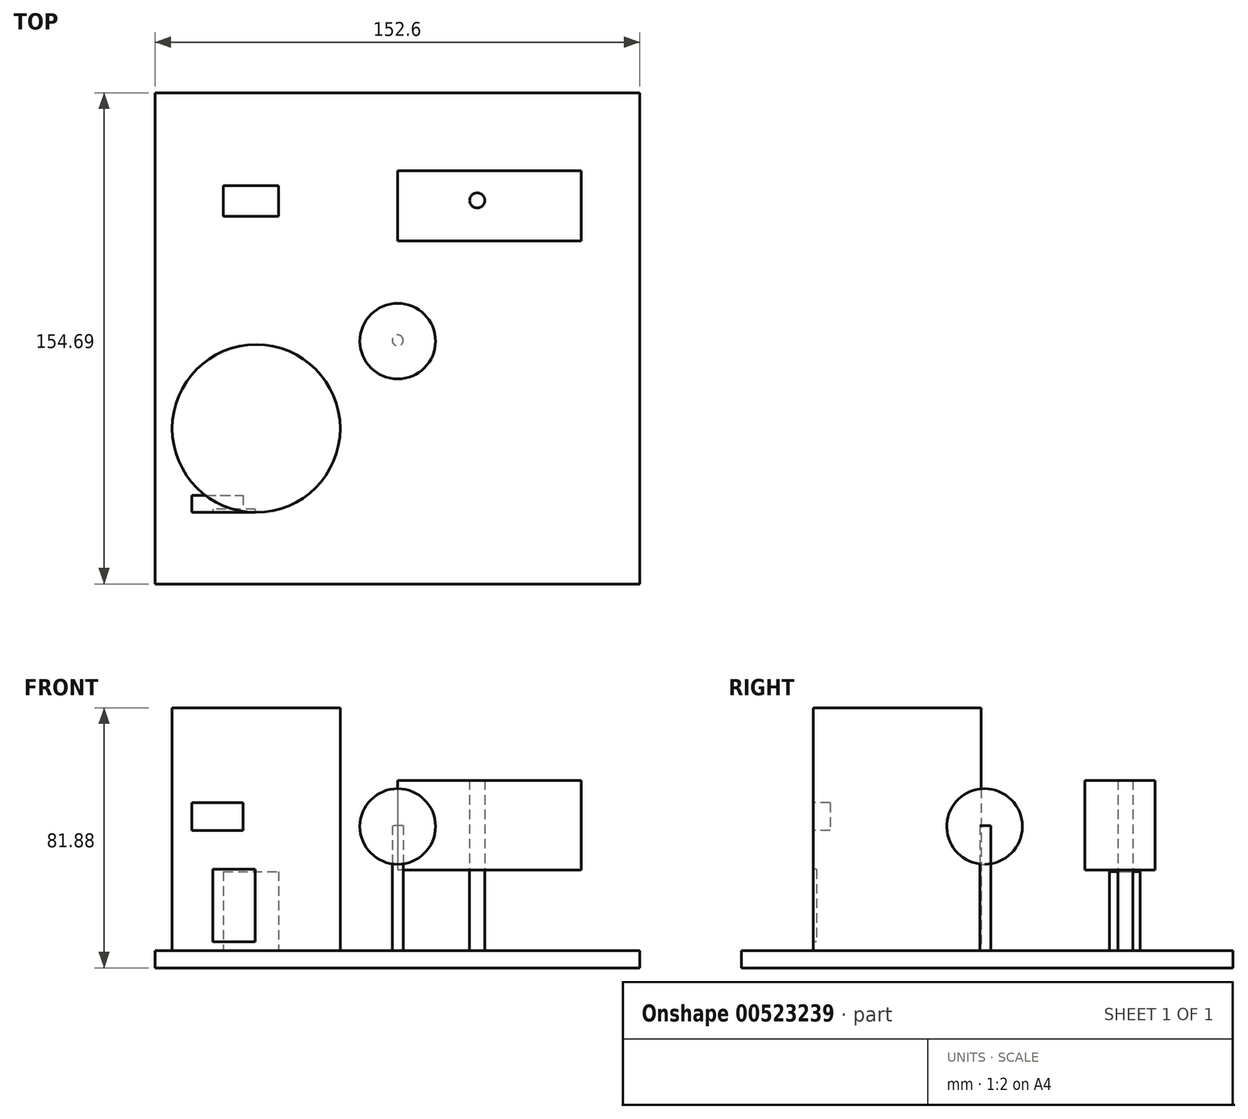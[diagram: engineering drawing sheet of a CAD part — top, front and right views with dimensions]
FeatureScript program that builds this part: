
annotation { "Feature Type Name" : "Feature", "Feature Type Description" : "" }
export const myFeature = defineFeature(function(context is Context, id is Id, definition is map)
    precondition{}
    {
        {
            var Q0;
            Q0=qCreatedBy(makeId("Front.planeOp"),FACE);
            var sketch = newSketch(context, id + "F0", { "sketchPlane" : qUnion([Q0])});
            skLineSegment(sketch, "E0.bottom", {"start": v(76.2, 0) * mm, "end": v(-76.39, 0) * mm});
            skLineSegment(sketch, "E0.top", {"start": v(76.2, -5.43) * mm, "end": v(-76.39, -5.43) * mm});
            skLineSegment(sketch, "E0.left", {"start": v(76.2, 0) * mm, "end": v(76.2, -5.43) * mm});
            skLineSegment(sketch, "E0.right", {"start": v(-76.39, 0) * mm, "end": v(-76.39, -5.43) * mm});
            skSolve(sketch);
        }
        {
            var Q0;
            Q0=makeQuery(id+"F0.imprint","IMPRINT",FACE,{"disambiguationData":[TD([[makeQuery(id+"F0.imprint","IMPRINT",EDGE,{"derivedFrom":sQuery(id+"F0.wireOp",EDGE,"E0.bottom")}),1.0]])]});
            extrude(context, id + "F1", {"entities" : qUnion([Q0]), "depth" : 78.74 * mm, "offsetDistance" : 25.4 * mm, "hasSecondDirection" : true, "secondDirectionOppositeDirection" : true, "secondDirectionDepth" : 75.95 * mm});
        }
        {
            var Q0;
            Q0=makeQuery(id+"F1.opExtrude","SWEPT_FACE",FACE,{"disambiguationData":[OSD([sQuery(id+"F0.wireOp",EDGE,"E0.bottom")])]});
            var sketch = newSketch(context, id + "F2", { "sketchPlane" : qUnion([Q0])});
            skCircle(sketch, "E1", {"center": v(0, -2) * mm, "radius": 1.72 * mm});
            skSolve(sketch);
        }
        {
            var Q0;
            Q0 = qSketchRegion(id + "F2", true);
            extrude(context, id + "F3", {"entities" : qUnion([Q0]), "depth" : 39.37 * mm, "offsetDistance" : 25.4 * mm});
        }
        {
            var Q0;
            Q0=qCreatedBy(makeId("Right.planeOp"),FACE);
            var sketch = newSketch(context, id + "F4", { "sketchPlane" : qUnion([Q0])});
            skArc(sketch, "E2", {"start": v(-2.25, 27.2) * mm, "mid": v(9.65, 39.1) * mm, "end": v(-2.25, 51) * mm});
            skLineSegment(sketch, "E3", {"start": v(-2.25, 39.1) * mm, "end": v(-2.25, 51) * mm});
            skLineSegment(sketch, "E4", {"start": v(-2.25, 39.1) * mm, "end": v(-2.25, 27.2) * mm});
            skSolve(sketch);
        }
        {
            var Q0;
            Q0=makeQuery(id+"F4.imprint","IMPRINT",FACE,{"disambiguationData":[TD([[makeQuery(id+"F4.imprint","IMPRINT",EDGE,{"derivedFrom":sQuery(id+"F4.wireOp",EDGE,"E2")}),1.0]])]});
            var Q1;
            Q1=sQuery(id+"F4.wireOp",EDGE,"E3");
            revolve(context, id + "F5", {"entities" : qUnion([Q0]), "axis" : qUnion([Q1]), "revolveType" : RevolveType.FULL});
        }
        {
            var Q0;
            Q0=makeQuery(id+"F1.opExtrude","SWEPT_FACE",FACE,{"disambiguationData":[OSD([sQuery(id+"F0.wireOp",EDGE,"E0.bottom")])]});
            var sketch = newSketch(context, id + "F6", { "sketchPlane" : qUnion([Q0])});
            skCircle(sketch, "E5", {"center": v(25.03, 42.07) * mm, "radius": 2.4 * mm});
            skSolve(sketch);
        }
        {
            var Q0;
            Q0 = qSketchRegion(id + "F6", true);
            extrude(context, id + "F7", {"entities" : qUnion([Q0]), "operationType" : NewBodyOperationType.ADD, "depth" : 25.4 * mm, "offsetDistance" : 25.4 * mm});
        }
        {
            var Q0;
            Q0=makeQuery(id+"F7.opExtrude","CAP_FACE",FACE,{"disambiguationData":[OSD([sQuery(id+"F6.wireOp",EDGE,"E5")])],"isStart":false});
            var sketch = newSketch(context, id + "F8", { "sketchPlane" : qUnion([Q0])});
            skLineSegment(sketch, "E6.bottom", {"start": v(57.79, 51.46) * mm, "end": v(0, 51.46) * mm});
            skLineSegment(sketch, "E6.top", {"start": v(57.79, 29.37) * mm, "end": v(0, 29.37) * mm});
            skLineSegment(sketch, "E6.left", {"start": v(57.79, 51.46) * mm, "end": v(57.79, 29.37) * mm});
            skLineSegment(sketch, "E6.right", {"start": v(0, 51.46) * mm, "end": v(0, 29.37) * mm});
            skSolve(sketch);
        }
        {
            var Q0;
            Q0=makeQuery(id+"F8.imprint","IMPRINT",FACE,{"disambiguationData":[TD([[makeQuery(id+"F8.imprint","IMPRINT",EDGE,{"derivedFrom":sQuery(id+"F8.wireOp",EDGE,"E6.bottom")}),1.0]])]});
            extrude(context, id + "F9", {"entities" : qUnion([Q0]), "depth" : 28.2 * mm, "offsetDistance" : 25.4 * mm});
        }
        {
            var Q0;
            Q0=makeQuery(id+"F1.opExtrude","SWEPT_FACE",FACE,{"disambiguationData":[OSD([sQuery(id+"F0.wireOp",EDGE,"E0.bottom")])]});
            var sketch = newSketch(context, id + "F10", { "sketchPlane" : qUnion([Q0])});
            skLineSegment(sketch, "E7.bottom", {"start": v(-54.84, 37.1) * mm, "end": v(-37.54, 37.1) * mm});
            skLineSegment(sketch, "E7.top", {"start": v(-54.84, 46.67) * mm, "end": v(-37.54, 46.67) * mm});
            skLineSegment(sketch, "E7.left", {"start": v(-54.84, 37.1) * mm, "end": v(-54.84, 46.67) * mm});
            skLineSegment(sketch, "E7.right", {"start": v(-37.54, 37.1) * mm, "end": v(-37.54, 46.67) * mm});
            skSolve(sketch);
        }
        {
            var Q0;
            Q0=makeQuery(id+"F10.imprint","IMPRINT",FACE,{"disambiguationData":[TD([[makeQuery(id+"F10.imprint","IMPRINT",EDGE,{"derivedFrom":sQuery(id+"F10.wireOp",EDGE,"E7.bottom")}),1.0]])]});
            extrude(context, id + "F11", {"entities" : qUnion([Q0]), "operationType" : NewBodyOperationType.ADD, "depth" : 24.9 * mm, "offsetDistance" : 25.4 * mm});
        }
        {
            var Q0;
            Q0=makeQuery(id+"F1.opExtrude","SWEPT_FACE",FACE,{"disambiguationData":[OSD([sQuery(id+"F0.wireOp",EDGE,"E0.bottom")])]});
            var sketch = newSketch(context, id + "F12", { "sketchPlane" : qUnion([Q0])});
            skCircle(sketch, "E8", {"center": v(-44.53, -29.77) * mm, "radius": 26.43 * mm});
            skSolve(sketch);
        }
        {
            var Q0;
            Q0=makeQuery(id+"F12.imprint","IMPRINT",FACE,{"disambiguationData":[TD([[makeQuery(id+"F12.imprint","IMPRINT",EDGE,{"derivedFrom":sQuery(id+"F12.wireOp",EDGE,"E8")}),1.0]])]});
            extrude(context, id + "F13", {"entities" : qUnion([Q0]), "operationType" : NewBodyOperationType.ADD, "depth" : 76.45 * mm, "offsetDistance" : 25.4 * mm});
        }
        {
            var Q0;
            Q0=makeQuery(id+"F13.opExtrude","CAP_FACE",FACE,{"disambiguationData":[OSD([sQuery(id+"F12.wireOp",EDGE,"E8")])],"isStart":false});
            var sketch = newSketch(context, id + "F14", { "sketchPlane" : qUnion([Q0])});
            skPoint(sketch, "E9", {"position": v(-44.78, -56.2) * mm});
            skSolve(sketch);
        }
        {
            var Q0;
            Q0=sQuery(id+"F14.wireOp",VERTEX,"E9");
            var Q1;
            Q1=qCreatedBy(makeId("Front.planeOp"),FACE);
            cPlane(context, id + "F15", {"entities" : qUnion([Q0, Q1]), "cplaneType" : CPlaneType.PLANE_POINT, "offset" : 25.4 * mm, "width" : 152.4 * mm, "height" : 152.4 * mm});
        }
        {
            var Q0;
            Q0=qCreatedBy(id+"F15.planeOp",FACE);
            var sketch = newSketch(context, id + "F16", { "sketchPlane" : qUnion([Q0])});
            skLineSegment(sketch, "E10.bottom", {"start": v(-44.81, 25.59) * mm, "end": v(-58.13, 25.59) * mm});
            skLineSegment(sketch, "E10.top", {"start": v(-44.81, 2.75) * mm, "end": v(-58.13, 2.75) * mm});
            skLineSegment(sketch, "E10.left", {"start": v(-44.81, 25.59) * mm, "end": v(-44.81, 2.75) * mm});
            skLineSegment(sketch, "E10.right", {"start": v(-58.13, 25.59) * mm, "end": v(-58.13, 2.75) * mm});
            skSolve(sketch);
        }
        {
            var Q0;
            Q0=makeQuery(id+"F16.imprint","IMPRINT",FACE,{"disambiguationData":[TD([[makeQuery(id+"F16.imprint","IMPRINT",EDGE,{"derivedFrom":sQuery(id+"F16.wireOp",EDGE,"E10.bottom")}),1.0]])]});
            extrude(context, id + "F17", {"entities" : qUnion([Q0]), "oppositeDirection" : true, "depth" : 1.02 * mm, "offsetDistance" : 25.4 * mm});
        }
        {
            var Q0;
            Q0=qCreatedBy(id+"F15.planeOp",FACE);
            var sketch = newSketch(context, id + "F18", { "sketchPlane" : qUnion([Q0])});
            skLineSegment(sketch, "E11.bottom", {"start": v(-64.79, 46.59) * mm, "end": v(-48.7, 46.59) * mm});
            skLineSegment(sketch, "E11.top", {"start": v(-64.79, 37.87) * mm, "end": v(-48.7, 37.87) * mm});
            skLineSegment(sketch, "E11.left", {"start": v(-64.79, 46.59) * mm, "end": v(-64.79, 37.87) * mm});
            skLineSegment(sketch, "E11.right", {"start": v(-48.7, 46.59) * mm, "end": v(-48.7, 37.87) * mm});
            skSolve(sketch);
        }
        {
            var Q0;
            Q0=makeQuery(id+"F18.imprint","IMPRINT",FACE,{"disambiguationData":[TD([[makeQuery(id+"F18.imprint","IMPRINT",EDGE,{"derivedFrom":sQuery(id+"F18.wireOp",EDGE,"E11.bottom")}),-1.0]])]});
            extrude(context, id + "F19", {"entities" : qUnion([Q0]), "oppositeDirection" : true, "depth" : 5.33 * mm, "offsetDistance" : 25.4 * mm});
        }
    });
